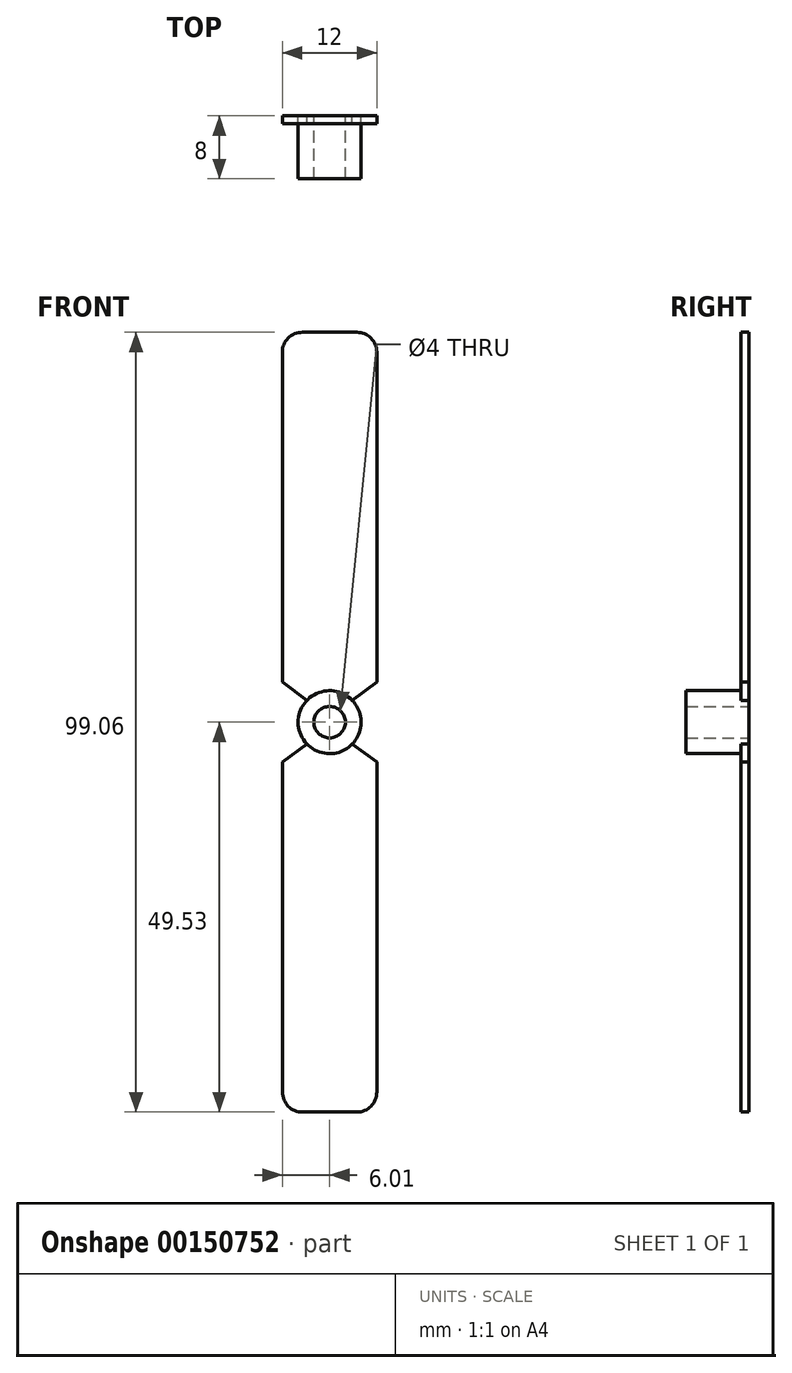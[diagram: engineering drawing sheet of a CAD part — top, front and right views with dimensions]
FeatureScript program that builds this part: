
annotation { "Feature Type Name" : "Feature", "Feature Type Description" : "" }
export const myFeature = defineFeature(function(context is Context, id is Id, definition is map)
    precondition{}
    {
        {
            var Q0;
            Q0=qCreatedBy(makeId("Front.planeOp"),FACE);
            var sketch = newSketch(context, id + "F0", { "sketchPlane" : qUnion([Q0])});
            skCircle(sketch, "E0", {"center": v(0, 0) * mm, "radius": 4 * mm});
            skCircle(sketch, "E1", {"center": v(0, 0) * mm, "radius": 2 * mm});
            skSolve(sketch);
        }
        {
            var Q0;
            Q0=makeQuery(id+"F0.imprint","IMPRINT",FACE,{"disambiguationData":[TD([[makeQuery(id+"F0.imprint","IMPRINT",EDGE,{"derivedFrom":sQuery(id+"F0.wireOp",EDGE,"E0")}),1.0]])]});
            extrude(context, id + "F1", {"entities" : qUnion([Q0]), "depth" : 8 * mm});
        }
        {
            var Q0;
            Q0=qCreatedBy(makeId("Front.planeOp"),FACE);
            var sketch = newSketch(context, id + "F2", { "sketchPlane" : qUnion([Q0])});
            skLineSegment(sketch, "E2.top", {"start": v(-6, 49.53) * mm, "end": v(6, 49.53) * mm});
            skLineSegment(sketch, "E2.left", {"start": v(-6, 5.08) * mm, "end": v(-6, 49.53) * mm});
            skLineSegment(sketch, "E2.right", {"start": v(6, 5.08) * mm, "end": v(6, 49.53) * mm});
            skLineSegment(sketch, "E3.top", {"start": v(-6, -49.53) * mm, "end": v(6, -49.53) * mm});
            skLineSegment(sketch, "E3.left", {"start": v(-6, -5.08) * mm, "end": v(-6, -49.53) * mm});
            skLineSegment(sketch, "E3.right", {"start": v(6, -5.08) * mm, "end": v(6, -49.53) * mm});
            skLineSegment(sketch, "E4", {"start": v(-6, 5.08) * mm, "end": v(-2.54, 2.54) * mm});
            skLineSegment(sketch, "E5", {"start": v(-2.54, 2.54) * mm, "end": v(2.54, 2.54) * mm});
            skLineSegment(sketch, "E6", {"start": v(2.54, 2.54) * mm, "end": v(6, 5.08) * mm});
            skLineSegment(sketch, "E7", {"start": v(-6, -5.08) * mm, "end": v(-2.54, -2.54) * mm});
            skLineSegment(sketch, "E8", {"start": v(-2.54, -2.54) * mm, "end": v(2.54, -2.54) * mm});
            skLineSegment(sketch, "E9", {"start": v(2.54, -2.54) * mm, "end": v(6, -5.08) * mm});
            skSolve(sketch);
        }
        {
            var Q0;
            Q0=makeQuery(id+"F2.imprint","IMPRINT",FACE,{"disambiguationData":[TD([[makeQuery(id+"F2.imprint","IMPRINT",EDGE,{"derivedFrom":sQuery(id+"F2.wireOp",EDGE,"E2.top")}),-1.0]])]});
            var Q1;
            Q1=makeQuery(id+"F2.imprint","IMPRINT",FACE,{"disambiguationData":[TD([[makeQuery(id+"F2.imprint","IMPRINT",EDGE,{"derivedFrom":sQuery(id+"F2.wireOp",EDGE,"E3.top")}),1.0]])]});
            extrude(context, id + "F3", {"entities" : qUnion([Q0, Q1]), "operationType" : NewBodyOperationType.ADD, "depth" : 1 * mm});
        }
        {
            var Q0;
            Q0=makeQuery(id+"F3.opExtrude","SWEPT_EDGE",EDGE,{"disambiguationData":[OSD([sQuery(id+"F2.wireOp",EDGE,"E2.top"),sQuery(id+"F2.wireOp",EDGE,"E2.left")])]});
            var Q1;
            Q1=makeQuery(id+"F3.opExtrude","SWEPT_EDGE",EDGE,{"disambiguationData":[OSD([sQuery(id+"F2.wireOp",EDGE,"E2.top"),sQuery(id+"F2.wireOp",EDGE,"E2.right")])]});
            var Q2;
            Q2=makeQuery(id+"F3.opExtrude","SWEPT_EDGE",EDGE,{"disambiguationData":[OSD([sQuery(id+"F2.wireOp",EDGE,"E3.top"),sQuery(id+"F2.wireOp",EDGE,"E3.right")])]});
            var Q3;
            Q3=makeQuery(id+"F3.opExtrude","SWEPT_EDGE",EDGE,{"disambiguationData":[OSD([sQuery(id+"F2.wireOp",EDGE,"E3.top"),sQuery(id+"F2.wireOp",EDGE,"E3.left")])]});
            fillet(context, id + "F4", {"entities" : qUnion([Q0, Q1, Q2, Q3]), "radius" : 2.54 * mm, "tangentPropagation" : true, "allowEdgeOverflow" : false});
        }
    });
